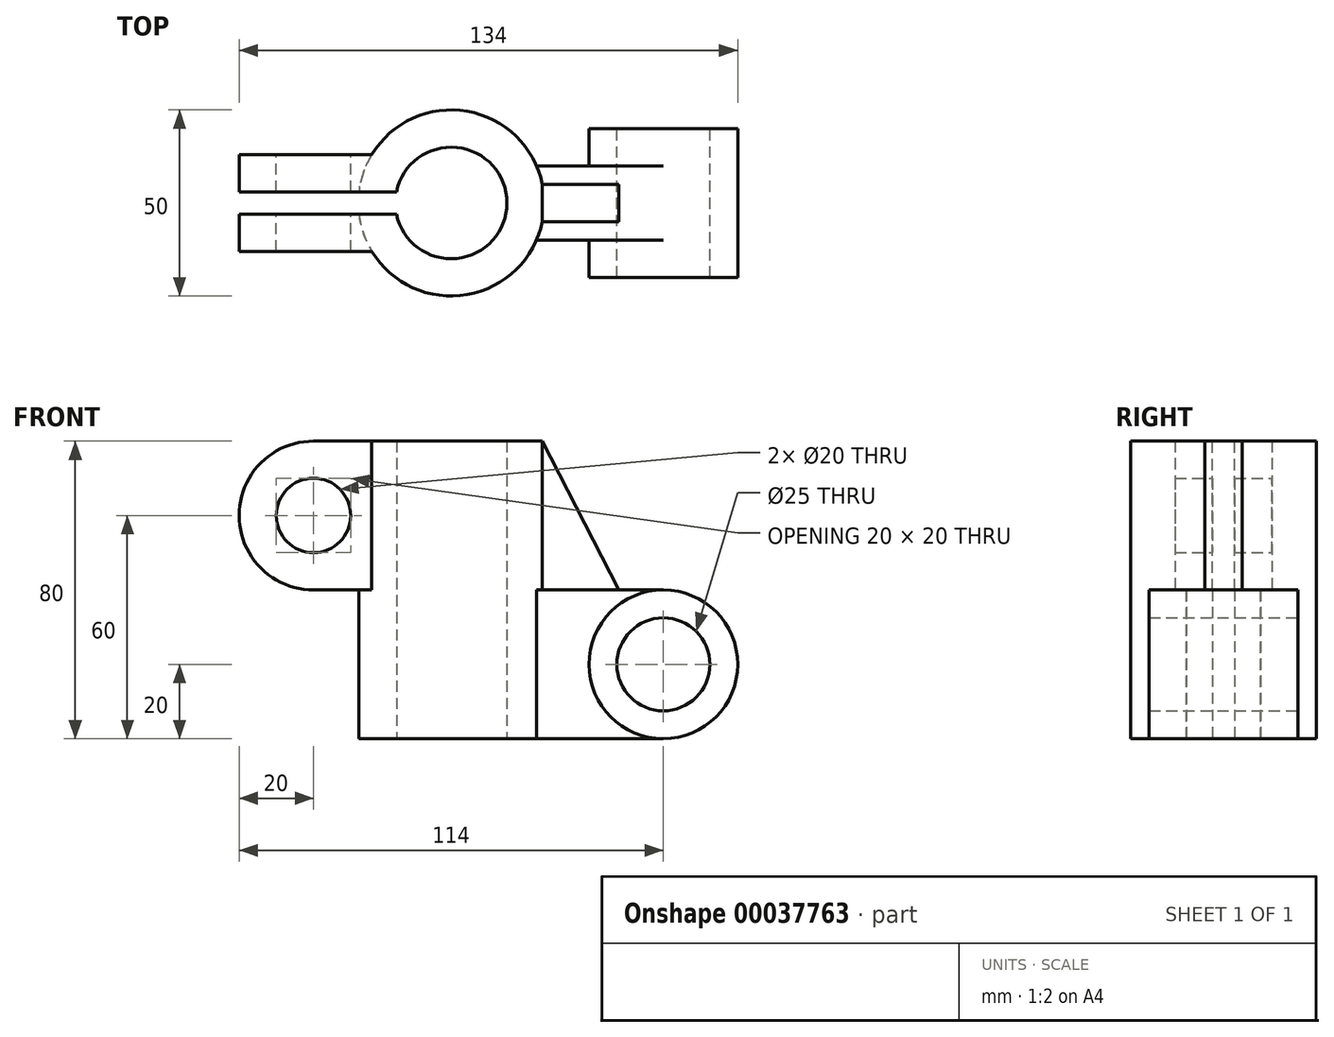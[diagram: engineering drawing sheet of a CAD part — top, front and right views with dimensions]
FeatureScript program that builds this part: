
annotation { "Feature Type Name" : "Feature", "Feature Type Description" : "" }
export const myFeature = defineFeature(function(context is Context, id is Id, definition is map)
    precondition{}
    {
        {
            var Q0;
            Q0=qCreatedBy(makeId("Top.planeOp"),FACE);
            var sketch = newSketch(context, id + "F0", { "sketchPlane" : qUnion([Q0])});
            skCircle(sketch, "E0", {"center": v(0, 0) * mm, "radius": 25 * mm});
            skCircle(sketch, "E1", {"center": v(0, 0) * mm, "radius": 15 * mm});
            skSolve(sketch);
        }
        {
            var Q0;
            Q0 = qSketchRegion(id + "F0", true);
            extrude(context, id + "F1", {"entities" : qUnion([Q0]), "depth" : 80 * mm, "symmetric" : true});
        }
        {
            var Q0;
            Q0=qCreatedBy(makeId("Front.planeOp"),FACE);
            var sketch = newSketch(context, id + "F2", { "sketchPlane" : qUnion([Q0])});
            skCircle(sketch, "E2", {"center": v(57, -20) * mm, "radius": 20 * mm});
            skCircle(sketch, "E3", {"center": v(57, -20) * mm, "radius": 12.5 * mm});
            skSolve(sketch);
        }
        {
            var Q0;
            Q0 = qSketchRegion(id + "F2", true);
            extrude(context, id + "F3", {"entities" : qUnion([Q0]), "depth" : 40 * mm, "symmetric" : true});
        }
        {
            var Q0;
            Q0=qCreatedBy(makeId("Front.planeOp"),FACE);
            var sketch = newSketch(context, id + "F4", { "sketchPlane" : qUnion([Q0])});
            skArc(sketch, "E4", {"start": v(-36.97, 40) * mm, "mid": v(-57, 20.01) * mm, "end": v(-37, 0) * mm});
            skLineSegment(sketch, "E5.0", {"start": v(-25, 40) * mm, "end": v(25, 40) * mm});
            skLineSegment(sketch, "E6", {"start": v(-37.03, 40) * mm, "end": v(-19.46, 40) * mm});
            skLineSegment(sketch, "E7", {"start": v(-19.46, 40) * mm, "end": v(-19.46, 0) * mm});
            skLineSegment(sketch, "E8", {"start": v(-19.46, 0) * mm, "end": v(-37, 0) * mm});
            skCircle(sketch, "E9", {"center": v(-37, 20) * mm, "radius": 10 * mm});
            skSolve(sketch);
        }
        {
            var Q0;
            Q0 = qSketchRegion(id + "F4", true);
            extrude(context, id + "F5", {"entities" : qUnion([Q0]), "operationType" : NewBodyOperationType.ADD, "depth" : 26 * mm, "symmetric" : true});
        }
        {
            var Q0;
            Q0=qCreatedBy(makeId("Right.planeOp"),FACE);
            cPlane(context, id + "F6", {"entities" : qUnion([Q0]), "cplaneType" : CPlaneType.OFFSET, "offset" : 30 * mm, "width" : 150 * mm, "height" : 150 * mm});
        }
        {
            var Q0;
            Q0=qCreatedBy(id+"F6.planeOp",FACE);
            var sketch = newSketch(context, id + "F7", { "sketchPlane" : qUnion([Q0])});
            skLineSegment(sketch, "E10.bottom", {"start": v(10, 0) * mm, "end": v(-10, 0) * mm});
            skLineSegment(sketch, "E10.top", {"start": v(10, -40) * mm, "end": v(-10, -40) * mm});
            skLineSegment(sketch, "E10.left", {"start": v(10, 0) * mm, "end": v(10, -40) * mm});
            skLineSegment(sketch, "E10.right", {"start": v(-10, 0) * mm, "end": v(-10, -40) * mm});
            skSolve(sketch);
        }
        {
            var Q0;
            Q0 = qSketchRegion(id + "F7", true);
            var Q1;
            Q1=makeQuery(id+"F1.opExtrude","SWEPT_FACE",FACE,{"disambiguationData":[OSD([sQuery(id+"F0.wireOp",EDGE,"E0")])]});
            var Q2;
            Q2=makeQuery(id+"F1.opExtrude","SWEPT_BODY",BODY,{"disambiguationData":[OSD([sQuery(id+"F0.wireOp",EDGE,"E0"),sQuery(id+"F0.wireOp",EDGE,"E1")])]});
            var Q3;
            Q3=makeQuery(id+"F3.opExtrude","SWEPT_FACE",FACE,{"disambiguationData":[OSD([sQuery(id+"F2.wireOp",EDGE,"E2")])]});
            var Q4;
            Q4=makeQuery(id+"F1.opExtrude","SWEPT_BODY",BODY,{"disambiguationData":[OSD([sQuery(id+"F0.wireOp",EDGE,"E0"),sQuery(id+"F0.wireOp",EDGE,"E1")])]});
            extrude(context, id + "F8", {"entities" : qUnion([Q0]), "operationType" : NewBodyOperationType.ADD, "endBound" : BoundingType.UP_TO_NEXT, "endBoundEntityFace" : qUnion([Q1]), "endBoundEntityBody" : qUnion([Q2]), "depth" : 25 * mm, "hasSecondDirection" : true, "secondDirectionBound" : BoundingType.UP_TO_BODY, "secondDirectionOppositeDirection" : true, "secondDirectionBoundEntityFace" : qUnion([Q3]), "secondDirectionBoundEntityBody" : qUnion([Q4]), "secondDirectionDepth" : 25 * mm});
        }
        {
            var Q0;
            Q0=makeQuery(id+"F1.opExtrude","CAP_FACE",FACE,{"disambiguationData":[OSD([sQuery(id+"F0.wireOp",EDGE,"E0"),sQuery(id+"F0.wireOp",EDGE,"E1")])],"isStart":false});
            var sketch = newSketch(context, id + "F9", { "sketchPlane" : qUnion([Q0])});
            skLineSegment(sketch, "E11.bottom", {"start": v(21.45, 5) * mm, "end": v(45, 5) * mm});
            skLineSegment(sketch, "E11.top", {"start": v(21.45, -5) * mm, "end": v(45, -5) * mm});
            skLineSegment(sketch, "E11.left", {"start": v(21.45, 5) * mm, "end": v(21.45, -5) * mm});
            skLineSegment(sketch, "E11.right", {"start": v(45, 5) * mm, "end": v(45, -5) * mm});
            skPoint(sketch, "E11.middle", {"position": v(33.23, 0) * mm});
            skSolve(sketch);
        }
        {
            var Q0;
            Q0 = qSketchRegion(id + "F9", true);
            var Q1;
            Q1=makeQuery(id+"F8.opExtrude","SWEPT_FACE",FACE,{"disambiguationData":[OSD([sQuery(id+"F7.wireOp",EDGE,"E10.bottom")])]});
            extrude(context, id + "F10", {"entities" : qUnion([Q0]), "operationType" : NewBodyOperationType.ADD, "endBound" : BoundingType.UP_TO_SURFACE, "oppositeDirection" : true, "endBoundEntityFace" : qUnion([Q1]), "depth" : 25 * mm});
        }
        {
            var Q0;
            Q0=makeQuery(id+"F10.opExtrude","SWEPT_FACE",FACE,{"disambiguationData":[OSD([sQuery(id+"F9.wireOp",EDGE,"E11.top")])]});
            var sketch = newSketch(context, id + "F11", { "sketchPlane" : qUnion([Q0])});
            skLineSegment(sketch, "E12", {"start": v(24.5, 40) * mm, "end": v(45, 0) * mm});
            skLineSegment(sketch, "E13", {"start": v(45, 0) * mm, "end": v(45, 40) * mm});
            skLineSegment(sketch, "E14", {"start": v(45, 40) * mm, "end": v(24.5, 40) * mm});
            skSolve(sketch);
        }
        {
            var Q0;
            Q0 = qSketchRegion(id + "F11", true);
            extrude(context, id + "F12", {"entities" : qUnion([Q0]), "operationType" : NewBodyOperationType.REMOVE, "endBound" : BoundingType.THROUGH_ALL, "oppositeDirection" : true, "depth" : 25 * mm});
        }
        {
            var Q0;
            Q0=makeQuery(id+"F10.boolean.opBoolean","MERGE",FACE,{"derivedFrom":[makeQuery(id+"F1.opExtrude","CAP_FACE",FACE,{"disambiguationData":[OSD([sQuery(id+"F0.wireOp",EDGE,"E0"),sQuery(id+"F0.wireOp",EDGE,"E1")])],"isStart":false}),makeQuery(id+"F10.opExtrude","CAP_FACE",FACE,{"disambiguationData":[OSD([sQuery(id+"F9.wireOp",EDGE,"E11.bottom"),sQuery(id+"F9.wireOp",EDGE,"E11.top"),sQuery(id+"F9.wireOp",EDGE,"E11.left"),sQuery(id+"F9.wireOp",EDGE,"E11.right")])],"isStart":true})]});
            var sketch = newSketch(context, id + "F13", { "sketchPlane" : qUnion([Q0])});
            skLineSegment(sketch, "E15.bottom", {"start": v(-12.01, 3) * mm, "end": v(-59.38, 3) * mm});
            skLineSegment(sketch, "E15.top", {"start": v(-12.01, -3) * mm, "end": v(-59.38, -3) * mm});
            skLineSegment(sketch, "E15.left", {"start": v(-12.01, 3) * mm, "end": v(-12.01, -3) * mm});
            skLineSegment(sketch, "E15.right", {"start": v(-59.38, 3) * mm, "end": v(-59.38, -3) * mm});
            skPoint(sketch, "E15.middle", {"position": v(-35.7, 0) * mm});
            skSolve(sketch);
        }
        {
            var Q0;
            Q0 = qSketchRegion(id + "F13", true);
            extrude(context, id + "F14", {"entities" : qUnion([Q0]), "operationType" : NewBodyOperationType.REMOVE, "endBound" : BoundingType.THROUGH_ALL, "oppositeDirection" : true, "depth" : 25 * mm});
        }
    });
